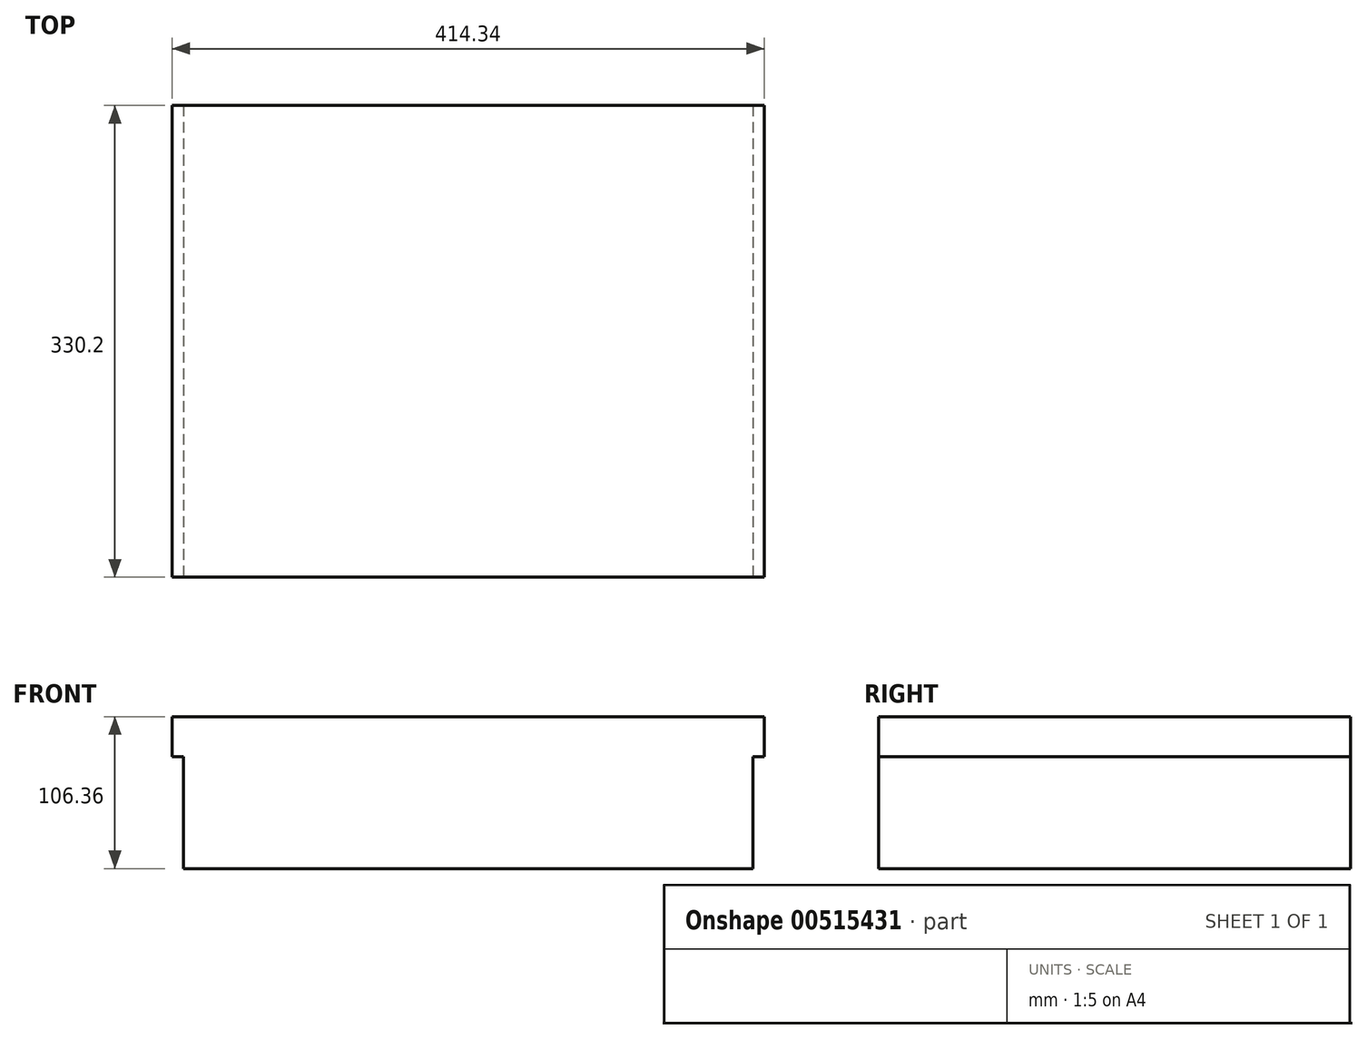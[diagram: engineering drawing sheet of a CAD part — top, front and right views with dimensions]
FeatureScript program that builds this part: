
annotation { "Feature Type Name" : "Feature", "Feature Type Description" : "" }
export const myFeature = defineFeature(function(context is Context, id is Id, definition is map)
    precondition{}
    {
        {
            var Q0;
            Q0=qCreatedBy(makeId("Front.planeOp"),FACE);
            var sketch = newSketch(context, id + "F0", { "sketchPlane" : qUnion([Q0])});
            skLineSegment(sketch, "E0.bottom", {"start": v(207.17, -53.18) * mm, "end": v(-207.17, -53.18) * mm, "construction": true});
            skLineSegment(sketch, "E0.top", {"start": v(207.17, 53.18) * mm, "end": v(-207.17, 53.18) * mm, "construction": true});
            skLineSegment(sketch, "E0.left", {"start": v(207.17, -53.18) * mm, "end": v(207.17, 53.18) * mm, "construction": true});
            skLineSegment(sketch, "E0.right", {"start": v(-207.17, -53.18) * mm, "end": v(-207.17, 53.18) * mm, "construction": true});
            skPoint(sketch, "E0.middle", {"position": v(0, 0) * mm});
            skLineSegment(sketch, "E1", {"start": v(0, 53.18) * mm, "end": v(0, -53.18) * mm, "construction": true});
            skLineSegment(sketch, "E2", {"start": v(0, 53.18) * mm, "end": v(-207.17, 53.18) * mm});
            skLineSegment(sketch, "E3", {"start": v(-207.17, 53.18) * mm, "end": v(-207.17, 25.24) * mm});
            skLineSegment(sketch, "E4", {"start": v(-207.17, 25.24) * mm, "end": v(-199.23, 25.24) * mm});
            skLineSegment(sketch, "E5", {"start": v(-199.23, 25.24) * mm, "end": v(-199.23, -53.18) * mm});
            skLineSegment(sketch, "E6", {"start": v(-199.23, -53.18) * mm, "end": v(0, -53.18) * mm});
            skLineSegment(sketch, "E7.MirrorCS", {"start": v(207.17, 25.24) * mm, "end": v(199.23, 25.24) * mm});
            skLineSegment(sketch, "E8.MirrorCS", {"start": v(199.23, -53.18) * mm, "end": v(0, -53.18) * mm});
            skLineSegment(sketch, "E9.MirrorCS", {"start": v(199.23, 25.24) * mm, "end": v(199.23, -53.18) * mm});
            skLineSegment(sketch, "E10.MirrorCS", {"start": v(207.17, 53.18) * mm, "end": v(207.17, 25.24) * mm});
            skLineSegment(sketch, "E11.MirrorCS", {"start": v(0, 53.18) * mm, "end": v(207.17, 53.18) * mm});
            skSolve(sketch);
        }
        {
            var Q0;
            Q0=makeQuery(id+"F0.imprint","IMPRINT",FACE,{"disambiguationData":[TD([[makeQuery(id+"F0.imprint","IMPRINT",EDGE,{"derivedFrom":sQuery(id+"F0.wireOp",EDGE,"E2")}),1.0]])]});
            extrude(context, id + "F1", {"entities" : qUnion([Q0]), "oppositeDirection" : true, "depth" : 330.2 * mm, "offsetDistance" : 25.4 * mm});
        }
    });
